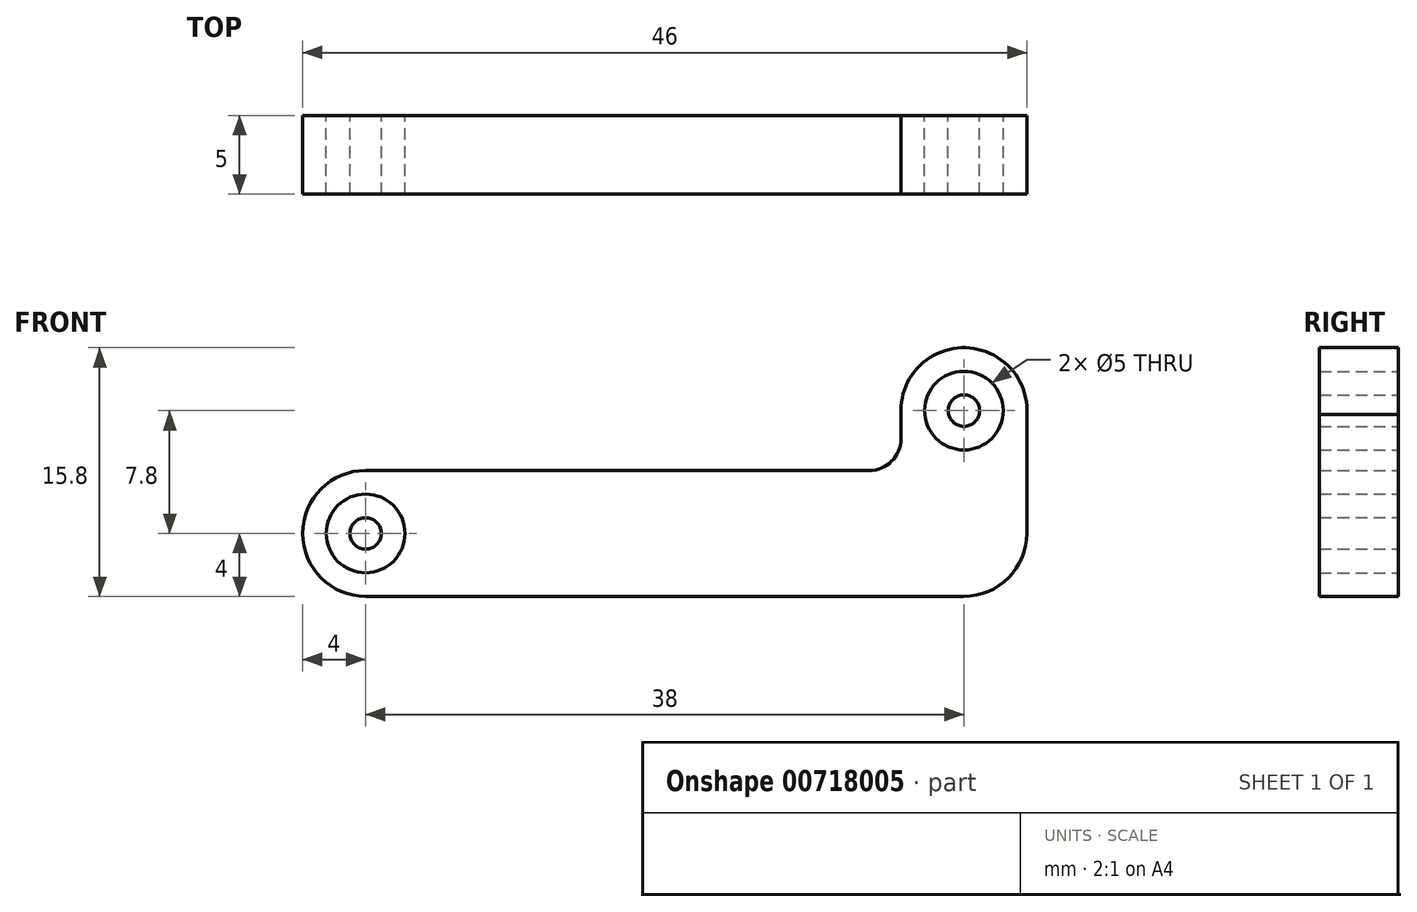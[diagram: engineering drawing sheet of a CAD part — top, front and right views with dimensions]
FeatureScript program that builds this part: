
annotation { "Feature Type Name" : "Feature", "Feature Type Description" : "" }
export const myFeature = defineFeature(function(context is Context, id is Id, definition is map)
    precondition{}
    {
        {
            var Q0;
            Q0=qCreatedBy(makeId("Front.planeOp"),FACE);
            var sketch = newSketch(context, id + "F0", { "sketchPlane" : qUnion([Q0])});
            skCircle(sketch, "E0", {"center": v(0, 0) * mm, "radius": 4 * mm});
            skCircle(sketch, "E1", {"center": v(0, 0) * mm, "radius": 2.5 * mm});
            skCircle(sketch, "E2", {"center": v(0, 0) * mm, "radius": 1 * mm});
            skCircle(sketch, "E3", {"center": v(38, 7.8) * mm, "radius": 4 * mm});
            skCircle(sketch, "E4", {"center": v(38, 7.8) * mm, "radius": 2.5 * mm});
            skCircle(sketch, "E5", {"center": v(38, 7.8) * mm, "radius": 1 * mm});
            skLineSegment(sketch, "E6", {"start": v(34, 7.8) * mm, "end": v(34, 6) * mm});
            skLineSegment(sketch, "E7", {"start": v(32, 4) * mm, "end": v(0, 4) * mm});
            skLineSegment(sketch, "E8", {"start": v(42, 8.04) * mm, "end": v(42, 0) * mm});
            skLineSegment(sketch, "E9", {"start": v(38, -4) * mm, "end": v(0, -4) * mm});
            skPoint(sketch, "E10.visualSharp", {"position": v(34, 4) * mm});
            skArc(sketch, "E10.filletArc", {"start": v(32, 4) * mm, "mid": v(33.41, 4.59) * mm, "end": v(34, 6) * mm});
            skPoint(sketch, "E11.visualSharp", {"position": v(42, -4) * mm});
            skArc(sketch, "E11.filletArc", {"start": v(38, -4) * mm, "mid": v(40.82, -2.83) * mm, "end": v(42, 0) * mm});
            skSolve(sketch);
        }
        {
            var Q0;
            Q0 = qSketchRegion(id + "F0", true);
            var Q1;
            Q1=makeQuery(id+"F0.imprint","IMPRINT",FACE,{"disambiguationData":[TD([[makeQuery(id+"F0.imprint","IMPRINT",EDGE,{"derivedFrom":sQuery(id+"F0.wireOp",EDGE,"E2")}),1.0]])]});
            var Q2;
            Q2=makeQuery(id+"F0.imprint","IMPRINT",FACE,{"disambiguationData":[TD([[makeQuery(id+"F0.imprint","IMPRINT",EDGE,{"derivedFrom":sQuery(id+"F0.wireOp",EDGE,"E5")}),1.0]])]});
            extrude(context, id + "F1", {"entities" : qUnion([Q0, Q1, Q2]), "depth" : 5 * mm, "offsetDistance" : 25 * mm});
        }
    });
